# Revit family: TC-Series-TC30-TC54
name_source: partatom
category: Mechanical Equipment
units: mm (PartAtom-declared; Revit-internal decimal feet)

## family parameters
Cut with Voids When Loaded = Yes
Host = Face
Part Type = Normal
Room Calculation Point = No
Round Connector Dimension = Use Diameter
Shared = Yes

## types (4) — shared parameters
Default Elevation = 4' - 0"
EFFICIENCY RATING = 0.00%
FLUE OFFSET FROM CENTER = 0' - 0"
FRAME MATERIAL = <By Category>
GAS PIPE CONNECTOR = 0' - 0 1/4"
HVAC BTU OUTPUT = 0 Btu/h
STAND OFF HEIGHT = 0' - 2"
UNIT WEIGHT = 0.00 kgf
flue connection size = 0' - 6"

## per-type parameters (varying)
| type | FACE HEIGHT | FACE WIDTH | FRAME HEIGHT | FRAME WIDTH | unit width |
| TC36 D2 | 2' - 8" | 3' - 1 3/4" | 3' - 5 5/16" | 4' - 0 1/16" | 3' - 6 1/4" |
| TC54 D2 | 3' - 7 3/8" | 4' - 6 1/16" | 5' - 3 7/8" | 5' - 3 1/2" | 4' - 10 9/16" |
| TC 42 D2 | 3' - 1 15/16" | 3' - 7 13/16" | 4' - 5 7/8" | 4' - 8 1/4" | 4' - 0 5/16" |
| TC30 D2 | 2' - 4" | 2' - 7 3/16" | 3' - 4 3/8" | 3' - 11 3/8" | 2' - 11 11/16" |

## geometry (parser evidence)
native form markers: Sweep x32
no freeform markers — native parametric forms only
